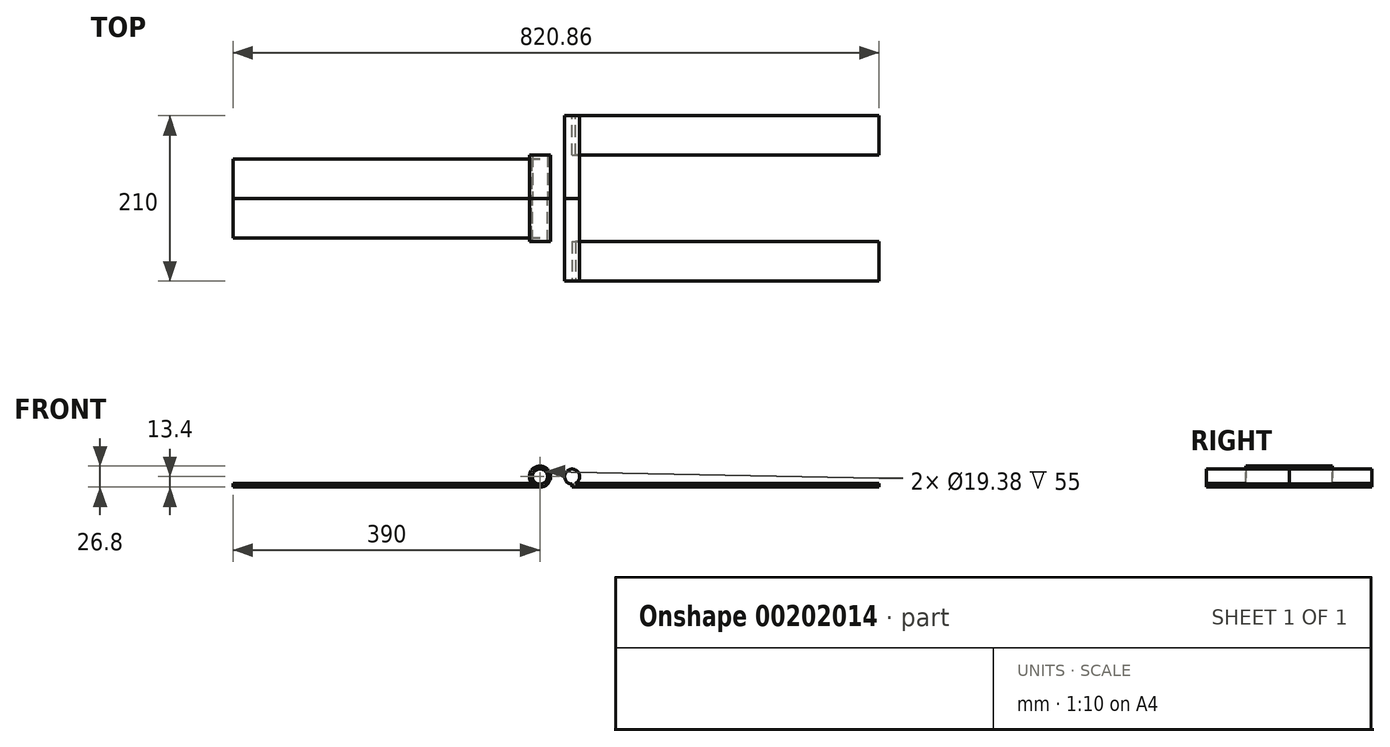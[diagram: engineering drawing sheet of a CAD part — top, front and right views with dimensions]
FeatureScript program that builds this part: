
annotation { "Feature Type Name" : "Feature", "Feature Type Description" : "" }
export const myFeature = defineFeature(function(context is Context, id is Id, definition is map)
    precondition{}
    {
        {
            var Q0;
            Q0=qCreatedBy(makeId("Front.planeOp"),FACE);
            var sketch = newSketch(context, id + "F0", { "sketchPlane" : qUnion([Q0])});
            skCircle(sketch, "E0", {"center": v(0, 0) * mm, "radius": 9.53 * mm});
            skSolve(sketch);
        }
        {
            var Q0;
            Q0=makeQuery(id+"F0.imprint","IMPRINT",FACE,{"disambiguationData":[TD([[makeQuery(id+"F0.imprint","IMPRINT",EDGE,{"derivedFrom":sQuery(id+"F0.wireOp",EDGE,"E0")}),1.0]])]});
            extrude(context, id + "F1", {"entities" : qUnion([Q0]), "depth" : 105 * mm});
        }
        {
            var Q0;
            Q0=qCreatedBy(makeId("Front.planeOp"),FACE);
            var sketch = newSketch(context, id + "F2", { "sketchPlane" : qUnion([Q0])});
            skCircle(sketch, "E1", {"center": v(-40.86, 0) * mm, "radius": 9.7 * mm});
            skCircle(sketch, "E2", {"center": v(-40.86, 0) * mm, "radius": 13.4 * mm});
            skSolve(sketch);
        }
        {
            var Q0;
            Q0=makeQuery(id+"F2.imprint","IMPRINT",FACE,{"disambiguationData":[TD([[makeQuery(id+"F2.imprint","IMPRINT",EDGE,{"derivedFrom":sQuery(id+"F2.wireOp",EDGE,"E1")}),-1.0]])]});
            extrude(context, id + "F3", {"entities" : qUnion([Q0]), "depth" : 55 * mm});
        }
        {
            var Q0;
            Q0=qCreatedBy(makeId("Front.planeOp"),FACE);
            var sketch = newSketch(context, id + "F4", { "sketchPlane" : qUnion([Q0])});
            skCircle(sketch, "E3.0", {"center": v(-40.86, 0) * mm, "radius": 13.4 * mm});
            skLineSegment(sketch, "E4", {"start": v(-40.86, -13.4) * mm, "end": v(-430.86, -13.4) * mm});
            skLineSegment(sketch, "E5", {"start": v(-430.86, -13.4) * mm, "end": v(-430.86, -8.4) * mm});
            skLineSegment(sketch, "E6", {"start": v(-430.86, -8.4) * mm, "end": v(-51.3, -8.4) * mm});
            skSolve(sketch);
        }
        {
            var Q0;
            {var subQ0=sQuery(id+"F4.wireOp",EDGE,"E4");Q0=makeQuery(id+"F4.imprint","IMPRINT",FACE,{"disambiguationData":[TD([[makeQuery(id+"F4.imprint","IMPRINT",EDGE,{"derivedFrom":subQ0}),-1.0]])]});}
            extrude(context, id + "F5", {"entities" : qUnion([Q0]), "operationType" : NewBodyOperationType.ADD, "depth" : 50 * mm});
        }
        {
            var Q0;
            Q0=makeQuery(id+"F1.opExtrude","CAP_FACE",FACE,{"disambiguationData":[OSD([sQuery(id+"F0.wireOp",EDGE,"E0")])],"isStart":false});
            var sketch = newSketch(context, id + "F6", { "sketchPlane" : qUnion([Q0])});
            skCircle(sketch, "E7.0", {"center": v(0, 0) * mm, "radius": 9.53 * mm});
            skLineSegment(sketch, "E8.0", {"start": v(-40.86, -13.4) * mm, "end": v(-430.86, -13.4) * mm});
            skLineSegment(sketch, "E9", {"start": v(0, -13.4) * mm, "end": v(390, -13.4) * mm});
            skLineSegment(sketch, "E10", {"start": v(390, -13.4) * mm, "end": v(390, -8.4) * mm});
            skLineSegment(sketch, "E11", {"start": v(390, -8.4) * mm, "end": v(4.5, -8.4) * mm});
            skLineSegment(sketch, "E12", {"start": v(0, -13.4) * mm, "end": v(0, -9.53) * mm});
            skSolve(sketch);
        }
        {
            var Q0;
            Q0=makeQuery(id+"F3.opExtrude","SWEPT_BODY",BODY,{"disambiguationData":[OSD([sQuery(id+"F2.wireOp",EDGE,"E1"),sQuery(id+"F2.wireOp",EDGE,"E2")])]});
            var Q1;
            Q1=qCreatedBy(makeId("Front.planeOp"),FACE);
            mirror(context, id + "F7", {"entities" : qUnion([Q0]), "mirrorPlane" : qUnion([Q1])});
        }
        {
            var Q0;
            Q0=makeQuery(id+"F6.imprint","IMPRINT",FACE,{"disambiguationData":[TD([[makeQuery(id+"F6.imprint","IMPRINT",EDGE,{"derivedFrom":sQuery(id+"F6.wireOp",EDGE,"E9")}),1.0]])]});
            extrude(context, id + "F8", {"entities" : qUnion([Q0]), "operationType" : NewBodyOperationType.ADD, "oppositeDirection" : true, "depth" : 50 * mm});
        }
        {
            var Q0;
            Q0=makeQuery(id+"F1.opExtrude","SWEPT_BODY",BODY,{"disambiguationData":[OSD([sQuery(id+"F0.wireOp",EDGE,"E0")])]});
            var Q1;
            Q1=qCreatedBy(makeId("Front.planeOp"),FACE);
            mirror(context, id + "F9", {"entities" : qUnion([Q0]), "mirrorPlane" : qUnion([Q1])});
        }
    });
